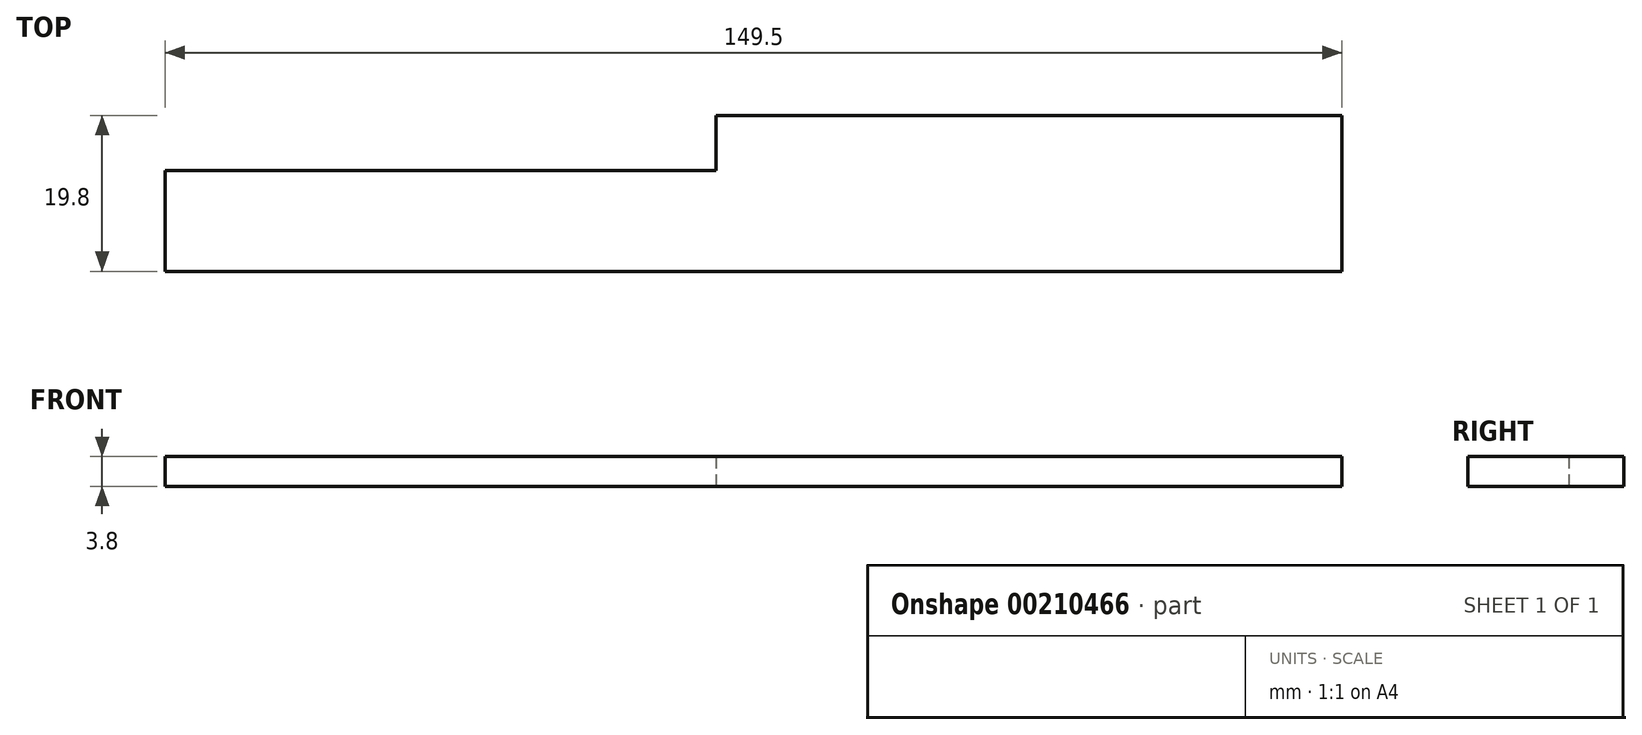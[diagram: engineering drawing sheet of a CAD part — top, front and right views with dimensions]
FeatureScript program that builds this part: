
annotation { "Feature Type Name" : "Feature", "Feature Type Description" : "" }
export const myFeature = defineFeature(function(context is Context, id is Id, definition is map)
    precondition{}
    {
        {
            var Q0;
            Q0=qCreatedBy(makeId("Top.planeOp"),FACE);
            var sketch = newSketch(context, id + "F0", { "sketchPlane" : qUnion([Q0])});
            skLineSegment(sketch, "E0.bottom", {"start": v(0, 0) * mm, "end": v(79.5, 0) * mm});
            skLineSegment(sketch, "E0.top", {"start": v(0, 19.8) * mm, "end": v(79.5, 19.8) * mm});
            skLineSegment(sketch, "E0.left", {"start": v(0, 0) * mm, "end": v(0, 19.8) * mm});
            skLineSegment(sketch, "E0.right", {"start": v(79.5, 0) * mm, "end": v(79.5, 19.8) * mm});
            skSolve(sketch);
        }
        {
            var Q0;
            Q0 = qSketchRegion(id + "F0", true);
            extrude(context, id + "F1", {"entities" : qUnion([Q0]), "depth" : 3.8 * mm});
        }
        {
            var Q0;
            Q0=makeQuery(id+"F1.opExtrude","SWEPT_FACE",FACE,{"disambiguationData":[OSD([sQuery(id+"F0.wireOp",EDGE,"E0.left")])]});
            var sketch = newSketch(context, id + "F2", { "sketchPlane" : qUnion([Q0])});
            skLineSegment(sketch, "E1", {"start": v(0, 0) * mm, "end": v(0, 3.8) * mm});
            skLineSegment(sketch, "E2", {"start": v(0, 3.8) * mm, "end": v(-12.8, 3.8) * mm});
            skLineSegment(sketch, "E3", {"start": v(-12.8, 3.8) * mm, "end": v(-12.8, 0) * mm});
            skPoint(sketch, "E3.endSnap0", {"position": v(-9.9, 0) * mm});
            skLineSegment(sketch, "E4", {"start": v(-12.8, 0) * mm, "end": v(0, 0) * mm});
            skSolve(sketch);
        }
        {
            var Q0;
            Q0 = qSketchRegion(id + "F2", true);
            extrude(context, id + "F3", {"entities" : qUnion([Q0]), "operationType" : NewBodyOperationType.ADD, "depth" : 70 * mm});
        }
    });
